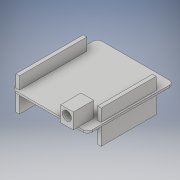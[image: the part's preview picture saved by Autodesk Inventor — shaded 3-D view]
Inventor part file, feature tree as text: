
AUTODESK INVENTOR PART (.ipt)
format: ipt  version: 2017 (Build 210142000, 142)  size: 171,008 bytes
history: native  units: in
note: dims shown in document units (in); Inventor stores cm internally (conversion verified against a paired STEP export)
features: extrude x5, sketch x5, fillet x1
ambient origin geometry x8: Origin, YZ Plane, XZ Plane, XY Plane, X Axis, Y Axis, Z Axis, Center Point
bodies: Solid1 (feature_tree)
feature tree (11):
  extrude  "Extrusion1"  Depth=2.371in
  fillet  "Fillet1"  Radius=0.055in
  extrude  "Extrusion2"  Depth=0.1in
  extrude  "Extrusion3"  Depth=1.514in
  extrude  "Extrusion4"  Depth=0.07in
  extrude  "Extrusion5"  Depth=0.425in
  sketch  "Sketch1"  dims[d0=2.1in d1=2.371in d2=0.055in d3=0.0in]
  sketch  "Sketch2"  dims[d4=0.125in d5=0.1in]
  sketch  "Sketch3"  dims[d6=0.1in d7=1.514in]
  sketch  "Sketch4"  dims[d8=1.8535in d9=0.07in]
  sketch  "Sketch5"  dims[d10=0.154in d11=0.425in d12=0.154in d17=0.34in d18=0.0in d19=0.348in d20=0.56in d21=0.14in d22=0.255in d23=0.4285in d24=0.0in d25=1.8535in d27=0.1in d28=1.514in d29=0.425in d30=0.154in d31=0.07in d32=0.518in d33=0.0in d34=0.25in d35=0.175in d36=0.25in d37=0.0in]
